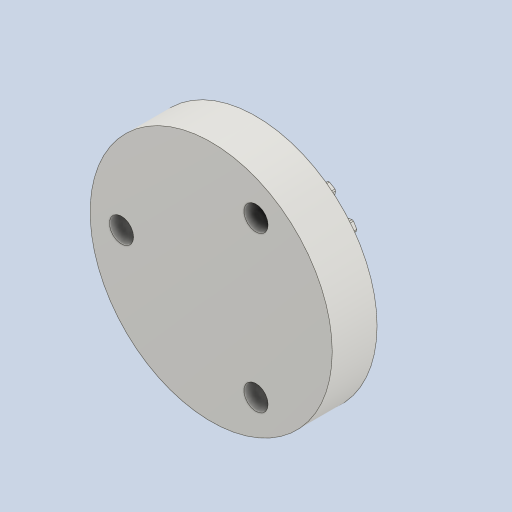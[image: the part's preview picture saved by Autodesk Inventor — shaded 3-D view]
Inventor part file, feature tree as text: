
AUTODESK INVENTOR PART (.ipt)
format: ipt  version: 2023 (Build 270158000, 158)  size: 306,176 bytes
history: native  units: mm (DEFAULTED — no unit token found)
features: extrude x3, plane x3, other x3, sketch x3, chamfer x1, fillet x1
ambient origin geometry x8: Origin, YZ Plane, XZ Plane, XY Plane, X Axis, Y Axis, Z Axis, Center Point
bodies: Solid1 (feature_tree)
feature tree (14):
  extrude  "Extrusion1"  Depth=5.0mm TaperAngle=0.0deg
  plane  "Work Plane2"
  plane  "Work Plane8"
  plane  "Work Plane9"
  other  "平歯車"
  sketch  "スケッチ5"
  extrude  "押し出し3"  Depth=10.0mm TaperAngle=0.0deg
  extrude  "押し出し4"  Depth=0.3mm
  chamfer  "面取り1"  Angle=15.0deg  [1 undecoded]
  fillet  "フィレット1"  [1 undecoded]
  sketch  "Sketch1"  dims[d0=14.0mm d1=5.0mm d2=0.0mm]
  sketch  "Sketch2"  dims[d3=12.0mm d4=10.0mm d5=0.0mm d16=12.0mm d17=0.0mm d34=15.0deg d39=0.0mm d41=0.0mm d43=12.0mm d46=12.0mm d47=0.0mm d48=0.0mm d51=27.0mm d52=5.0mm d53=2.7mm d54=10.0mm d55=30.0mm d57=360.0deg d59=5.0mm d60=0.0mm d61=3.0mm d62=0.0mm d63=0.1mm d64=2.0mm d65=45.0deg d66=0.3mm]
  other  "Srf1"
  other  "ピッチ円直径"
note: 2 required parameter values undecoded (feature->parameter linkage not recoverable at this tier; creation-order binding heuristic only, values carry confidence <= 0.55)
